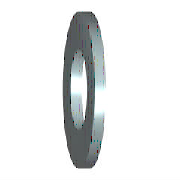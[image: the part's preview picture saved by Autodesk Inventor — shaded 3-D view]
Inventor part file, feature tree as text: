
AUTODESK INVENTOR PART (.ipt)
format: ipt  version: 2014 SP1 (Build 180222100, 222)  size: 105,472 bytes
history: native  units: mm (DEFAULTED — no unit token found)
features: other x1, plane x1, sketch x1
ambient origin geometry x7: Origin, YZ Plane, XY Plane, X Axis, Y Axis, Z Axis, Center Point
bodies: Solid1 (feature_tree), Body (feature_tree)
feature tree (3):
  other  "Work Axis1"
  plane  "Work Plane1"
  sketch  "Sketch"  dims[d0=3.2mm d1=7.0mm d2=0.5mm d3=0.0mm d4=0.0mm d5=0.0mm d6=0.0mm d7=0.0mm]
